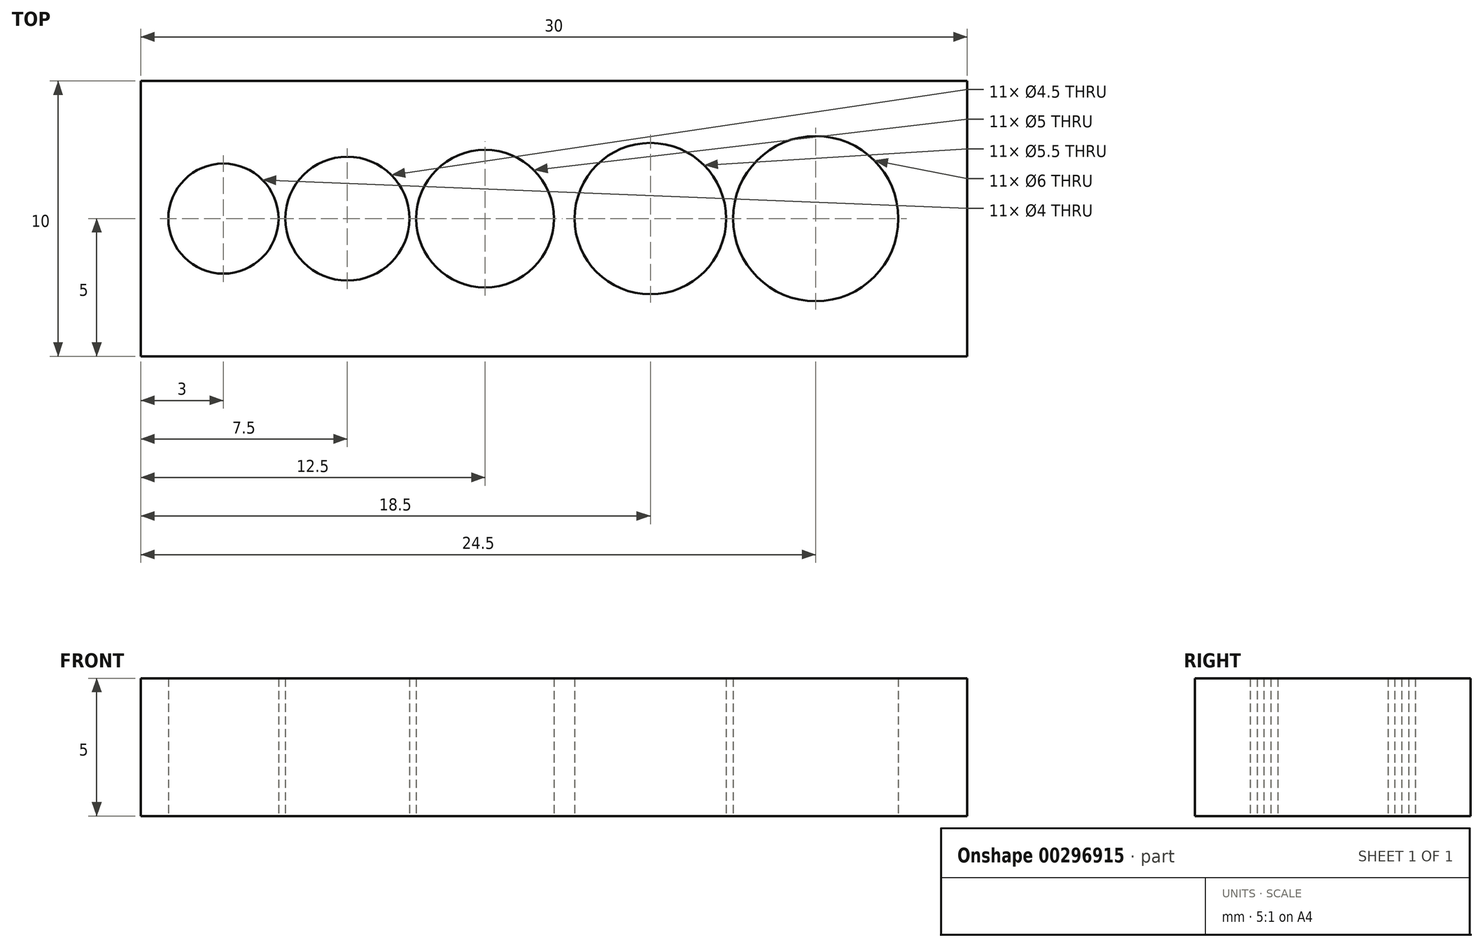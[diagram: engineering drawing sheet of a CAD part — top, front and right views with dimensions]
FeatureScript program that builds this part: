
annotation { "Feature Type Name" : "Feature", "Feature Type Description" : "" }
export const myFeature = defineFeature(function(context is Context, id is Id, definition is map)
    precondition{}
    {
        {
            var Q0;
            Q0=qCreatedBy(makeId("Top.planeOp"),FACE);
            var sketch = newSketch(context, id + "F0", { "sketchPlane" : qUnion([Q0])});
            skLineSegment(sketch, "E0", {"start": v(0, 0) * mm, "end": v(0, 10) * mm});
            skLineSegment(sketch, "E1", {"start": v(0, 10) * mm, "end": v(30, 10) * mm});
            skLineSegment(sketch, "E2", {"start": v(30, 10) * mm, "end": v(30, 0) * mm});
            skLineSegment(sketch, "E3", {"start": v(30, 0) * mm, "end": v(0, 0) * mm});
            skLineSegment(sketch, "E4", {"start": v(3, 0) * mm, "end": v(3, 5) * mm});
            skCircle(sketch, "E5", {"center": v(3, 5) * mm, "radius": 2 * mm});
            skLineSegment(sketch, "E6", {"start": v(3, 5) * mm, "end": v(0, 5) * mm});
            skLineSegment(sketch, "E7", {"start": v(3, 5) * mm, "end": v(7.5, 5) * mm});
            skCircle(sketch, "E8", {"center": v(7.5, 5) * mm, "radius": 2.25 * mm});
            skLineSegment(sketch, "E9", {"start": v(7.5, 5) * mm, "end": v(12.5, 5) * mm});
            skLineSegment(sketch, "E10", {"start": v(12.5, 5) * mm, "end": v(18.5, 5) * mm});
            skCircle(sketch, "E11", {"center": v(12.5, 5) * mm, "radius": 2.5 * mm});
            skCircle(sketch, "E12", {"center": v(18.5, 5) * mm, "radius": 2.75 * mm});
            skLineSegment(sketch, "E13", {"start": v(18.5, 5) * mm, "end": v(24.5, 5) * mm});
            skCircle(sketch, "E14", {"center": v(24.5, 5) * mm, "radius": 3 * mm});
            skSolve(sketch);
        }
        {
            var Q0;
            {var subQ15=sQuery(id+"F0.wireOp",EDGE,"E1");Q0=makeQuery(id+"F0.imprint","IMPRINT",FACE,{"disambiguationData":[TD([[makeQuery(id+"F0.imprint","IMPRINT",EDGE,{"derivedFrom":subQ15}),-1.0]])]});}
            var Q1;
            {var subQ5=sQuery(id+"F0.wireOp",EDGE,"E3");var subQ7=sQuery(id+"F0.wireOp",EDGE,"E0");var subQ8=makeQuery(id+"F0.imprint","INTERSECT",VERTEX,{"derivedFrom":[subQ7,subQ5]});Q1=makeQuery(id+"F0.imprint","IMPRINT",FACE,{"disambiguationData":[TD([[makeQuery(id+"F0.imprint","IMPRINT",EDGE,{"disambiguationData":[TD([[subQ8,-1.0]])],"derivedFrom":subQ7}),-1.0]])]});}
            extrude(context, id + "F1", {"entities" : qUnion([Q0, Q1]), "depth" : 5 * mm});
        }
    });
